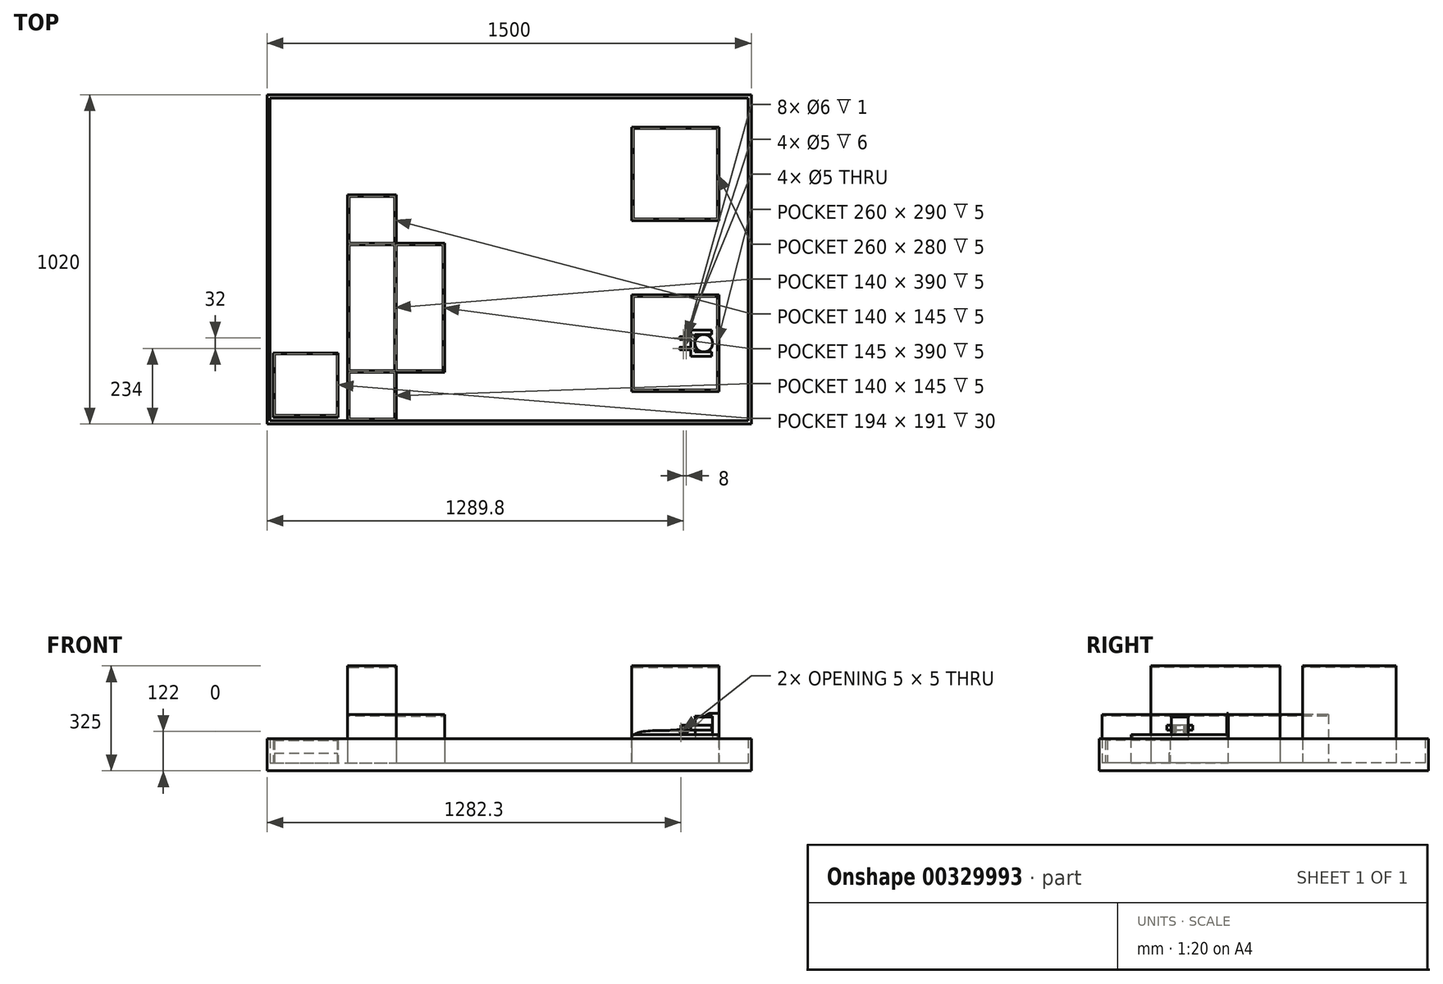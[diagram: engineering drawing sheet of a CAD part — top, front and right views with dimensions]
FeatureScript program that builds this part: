
annotation { "Feature Type Name" : "Feature", "Feature Type Description" : "" }
export const myFeature = defineFeature(function(context is Context, id is Id, definition is map)
    precondition{}
    {
        {
            var Q0;
            Q0=qCreatedBy(makeId("Top.planeOp"),FACE);
            var sketch = newSketch(context, id + "F0", { "sketchPlane" : qUnion([Q0])});
            skCircle(sketch, "E0", {"center": v(0, 0) * mm, "radius": 27.2 * mm});
            skSolve(sketch);
        }
        {
            var Q0;
            Q0=qSketchRegion(id+"F0",true);
            extrude(context, id + "F1", {"entities" : qUnion([Q0]), "depth" : 2.83 * mm});
        }
        {
            var Q0;
            Q0=makeQuery(id+"F1.opExtrude","CAP_FACE",FACE,{"disambiguationData":[OSD([sQuery(id+"F0.wireOp",EDGE,"E0")])],"isStart":false});
            var sketch = newSketch(context, id + "F2", { "sketchPlane" : qUnion([Q0])});
            skCircle(sketch, "E1", {"center": v(0, 0) * mm, "radius": 26.4 * mm});
            skSolve(sketch);
        }
        {
            var Q0;
            Q0=qSketchRegion(id+"F2",true);
            extrude(context, id + "F3", {"entities" : qUnion([Q0]), "operationType" : NewBodyOperationType.ADD, "depth" : 67.36 * mm});
        }
        {
            var Q0;
            Q0=makeQuery(id+"F3.opExtrude","CAP_FACE",FACE,{"disambiguationData":[OSD([sQuery(id+"F2.wireOp",EDGE,"E1")])],"isStart":false});
            var sketch = newSketch(context, id + "F4", { "sketchPlane" : qUnion([Q0])});
            skCircle(sketch, "E2", {"center": v(0, 0) * mm, "radius": 27.2 * mm});
            skSolve(sketch);
        }
        {
            var Q0;
            Q0=qSketchRegion(id+"F4",true);
            extrude(context, id + "F5", {"entities" : qUnion([Q0]), "operationType" : NewBodyOperationType.ADD, "depth" : 2.83 * mm});
        }
        {
            var Q0;
            Q0=makeQuery(id+"F5.opExtrude","CAP_FACE",FACE,{"disambiguationData":[OSD([sQuery(id+"F4.wireOp",EDGE,"E2")])],"isStart":false});
            var sketch = newSketch(context, id + "F6", { "sketchPlane" : qUnion([Q0])});
            skSolve(sketch);
        }
        {
            var Q0;
            Q0=qCreatedBy(makeId("Top.planeOp"),FACE);
            cPlane(context, id + "F7", {"entities" : qUnion([Q0]), "cplaneType" : CPlaneType.OFFSET, "offset" : 25 * mm, "width" : 150 * mm, "height" : 150 * mm});
        }
        {
            var Q0;
            Q0=makeQuery(id+"F6.imprint","IMPRINT",FACE,{"disambiguationData":[TD([[makeQuery(id+"F6.imprint","IMPRINT",EDGE,{"derivedFrom":makeQuery(id+"F5.opExtrude","CAP_EDGE",EDGE,{"disambiguationData":[OSD([sQuery(id+"F4.wireOp",EDGE,"E2")])],"isStart":false})}),1.0]])]});
            var sketch = newSketch(context, id + "F8", { "sketchPlane" : qUnion([Q0])});
            skSolve(sketch);
        }
        {
            var Q0;
            Q0=qCreatedBy(makeId("Top.planeOp"),FACE);
            var sketch = newSketch(context, id + "F9", { "sketchPlane" : qUnion([Q0])});
            skLineSegment(sketch, "E3.bottom", {"start": v(-222.8, -150) * mm, "end": v(47.2, -150) * mm});
            skLineSegment(sketch, "E3.top", {"start": v(-222.8, 150) * mm, "end": v(47.2, 150) * mm});
            skLineSegment(sketch, "E3.left", {"start": v(-222.8, -150) * mm, "end": v(-222.8, 150) * mm});
            skLineSegment(sketch, "E3.right", {"start": v(47.2, -150) * mm, "end": v(47.2, 150) * mm});
            skSolve(sketch);
        }
        {
            var Q0;
            Q0=qSketchRegion(id+"F9",true);
            extrude(context, id + "F10", {"entities" : qUnion([Q0]), "oppositeDirection" : true, "depth" : 72 * mm});
        }
        {
            var Q0;
            Q0=makeQuery(id+"F10.opExtrude","CAP_FACE",FACE,{"disambiguationData":[OSD([sQuery(id+"F9.wireOp",EDGE,"E3.bottom"),sQuery(id+"F9.wireOp",EDGE,"E3.top"),sQuery(id+"F9.wireOp",EDGE,"E3.left"),sQuery(id+"F9.wireOp",EDGE,"E3.right")])],"isStart":true});
            var sketch = newSketch(context, id + "F11", { "sketchPlane" : qUnion([Q0])});
            skLineSegment(sketch, "E4.bottom", {"start": v(-222.8, -150) * mm, "end": v(47.2, -150) * mm});
            skLineSegment(sketch, "E4.top", {"start": v(-222.8, -145) * mm, "end": v(42.2, -145) * mm});
            skLineSegment(sketch, "E4.left", {"start": v(-222.8, -150) * mm, "end": v(-222.8, -145) * mm});
            skLineSegment(sketch, "E5.bottom", {"start": v(47.2, 150) * mm, "end": v(42.2, 150) * mm});
            skLineSegment(sketch, "E5.left", {"start": v(47.2, 150) * mm, "end": v(47.2, -150) * mm});
            skLineSegment(sketch, "E5.right", {"start": v(42.2, 150) * mm, "end": v(42.2, -145) * mm});
            skSolve(sketch);
        }
        {
            var Q0;
            Q0=qSketchRegion(id+"F11",true);
            extrude(context, id + "F12", {"entities" : qUnion([Q0]), "operationType" : NewBodyOperationType.ADD, "depth" : 15 * mm});
        }
        {
            var Q0;
            Q0=makeQuery(id+"F12.boolean.opBoolean","MERGE",FACE,{"derivedFrom":[makeQuery(id+"F10.opExtrude","SWEPT_FACE",FACE,{"disambiguationData":[OSD([sQuery(id+"F9.wireOp",EDGE,"E3.top")])]}),makeQuery(id+"F12.opExtrude","SWEPT_FACE",FACE,{"disambiguationData":[OSD([sQuery(id+"F11.wireOp",EDGE,"E5.bottom")])]})]});
            var sketch = newSketch(context, id + "F13", { "sketchPlane" : qUnion([Q0])});
            skLineSegment(sketch, "E6", {"start": v(-47.2, 81.36) * mm, "end": v(-21.31, 81.36) * mm});
            skFitSpline(sketch, "E7", {"points": [v(-21.31, 81.36) * mm, v(15.24, 52.01) * mm, v(114.14, 28.17) * mm, v(222.8, 0) * mm], "startDerivative": vector(181.02, 0.3) * mm, "endDerivative": vector(-1.73, -239.85) * mm});
            skLineSegment(sketch, "E8", {"start": v(-47.2, 81.36) * mm, "end": v(-47.2, -72) * mm});
            skLineSegment(sketch, "E9", {"start": v(-47.2, -72) * mm, "end": v(222.8, -72) * mm});
            skLineSegment(sketch, "E10", {"start": v(222.8, -72) * mm, "end": v(222.8, 0) * mm});
            skSolve(sketch);
        }
        {
            var Q0;
            Q0=qSketchRegion(id+"F13",true);
            extrude(context, id + "F14", {"entities" : qUnion([Q0]), "operationType" : NewBodyOperationType.ADD, "oppositeDirection" : true, "depth" : 5 * mm});
        }
        {
            var Q0;
            Q0=makeQuery(id+"F10.opExtrude","CAP_FACE",FACE,{"disambiguationData":[OSD([sQuery(id+"F9.wireOp",EDGE,"E3.bottom"),sQuery(id+"F9.wireOp",EDGE,"E3.top"),sQuery(id+"F9.wireOp",EDGE,"E3.left"),sQuery(id+"F9.wireOp",EDGE,"E3.right")])],"isStart":true});
            var sketch = newSketch(context, id + "F15", { "sketchPlane" : qUnion([Q0])});
            skLineSegment(sketch, "E11.bottom", {"start": v(-222.8, 145) * mm, "end": v(-217.8, 145) * mm});
            skLineSegment(sketch, "E11.top", {"start": v(-222.8, -145) * mm, "end": v(-217.8, -145) * mm});
            skLineSegment(sketch, "E11.left", {"start": v(-222.8, 145) * mm, "end": v(-222.8, -145) * mm});
            skLineSegment(sketch, "E11.right", {"start": v(-217.8, 145) * mm, "end": v(-217.8, -145) * mm});
            skSolve(sketch);
        }
        {
            var Q0;
            Q0=qSketchRegion(id+"F15",true);
            extrude(context, id + "F16", {"entities" : qUnion([Q0]), "operationType" : NewBodyOperationType.ADD, "depth" : 5 * mm});
        }
        {
            var Q0;
            Q0=makeQuery(id+"F10.opExtrude","CAP_FACE",FACE,{"disambiguationData":[OSD([sQuery(id+"F9.wireOp",EDGE,"E3.bottom"),sQuery(id+"F9.wireOp",EDGE,"E3.top"),sQuery(id+"F9.wireOp",EDGE,"E3.left"),sQuery(id+"F9.wireOp",EDGE,"E3.right")])],"isStart":false});
            var sketch = newSketch(context, id + "F17", { "sketchPlane" : qUnion([Q0])});
            skLineSegment(sketch, "E12.bottom", {"start": v(147.2, 250) * mm, "end": v(-1352.8, 250) * mm});
            skLineSegment(sketch, "E12.top", {"start": v(147.2, -770) * mm, "end": v(-1352.8, -770) * mm});
            skLineSegment(sketch, "E12.left", {"start": v(147.2, 250) * mm, "end": v(147.2, -770) * mm});
            skLineSegment(sketch, "E12.right", {"start": v(-1352.8, 250) * mm, "end": v(-1352.8, -770) * mm});
            skSolve(sketch);
        }
        {
            var Q0;
            Q0=qSketchRegion(id+"F17",true);
            extrude(context, id + "F18", {"entities" : qUnion([Q0]), "operationType" : NewBodyOperationType.ADD, "depth" : 25 * mm});
        }
        {
            var Q0;
            Q0=makeQuery(id+"F18.opExtrude","CAP_FACE",FACE,{"disambiguationData":[OSD([sQuery(id+"F17.wireOp",EDGE,"E12.bottom"),sQuery(id+"F17.wireOp",EDGE,"E12.top"),sQuery(id+"F17.wireOp",EDGE,"E12.left"),sQuery(id+"F17.wireOp",EDGE,"E12.right")])],"isStart":true});
            var sketch = newSketch(context, id + "F19", { "sketchPlane" : qUnion([Q0])});
            skLineSegment(sketch, "E13.bottom", {"start": v(-222.8, 670) * mm, "end": v(47.2, 670) * mm});
            skLineSegment(sketch, "E13.top", {"start": v(-222.8, 380) * mm, "end": v(47.2, 380) * mm});
            skLineSegment(sketch, "E13.left", {"start": v(-222.8, 670) * mm, "end": v(-222.8, 380) * mm});
            skLineSegment(sketch, "E13.right", {"start": v(47.2, 670) * mm, "end": v(47.2, 380) * mm});
            skSolve(sketch);
        }
        {
            var Q0;
            Q0=qSketchRegion(id+"F19",true);
            extrude(context, id + "F20", {"entities" : qUnion([Q0]), "operationType" : NewBodyOperationType.ADD, "depth" : 300 * mm});
        }
        {
            var Q0;
            Q0=makeQuery(id+"F20.opExtrude","CAP_FACE",FACE,{"disambiguationData":[OSD([sQuery(id+"F19.wireOp",EDGE,"E13.bottom"),sQuery(id+"F19.wireOp",EDGE,"E13.top"),sQuery(id+"F19.wireOp",EDGE,"E13.left"),sQuery(id+"F19.wireOp",EDGE,"E13.right")])],"isStart":false});
            var sketch = newSketch(context, id + "F21", { "sketchPlane" : qUnion([Q0])});
            skLineSegment(sketch, "E14.bottom", {"start": v(-217.8, 665) * mm, "end": v(42.2, 665) * mm});
            skLineSegment(sketch, "E14.top", {"start": v(-217.8, 385) * mm, "end": v(42.2, 385) * mm});
            skLineSegment(sketch, "E14.left", {"start": v(-217.8, 665) * mm, "end": v(-217.8, 385) * mm});
            skLineSegment(sketch, "E14.right", {"start": v(42.2, 665) * mm, "end": v(42.2, 385) * mm});
            skSolve(sketch);
        }
        {
            var Q0;
            Q0=qSketchRegion(id+"F21",true);
            extrude(context, id + "F22", {"entities" : qUnion([Q0]), "operationType" : NewBodyOperationType.REMOVE, "oppositeDirection" : true, "depth" : 5 * mm});
        }
        {
            var Q0;
            Q0=makeQuery(id+"F18.opExtrude","CAP_FACE",FACE,{"disambiguationData":[OSD([sQuery(id+"F17.wireOp",EDGE,"E12.bottom"),sQuery(id+"F17.wireOp",EDGE,"E12.top"),sQuery(id+"F17.wireOp",EDGE,"E12.left"),sQuery(id+"F17.wireOp",EDGE,"E12.right")])],"isStart":true});
            var sketch = newSketch(context, id + "F23", { "sketchPlane" : qUnion([Q0])});
            skLineSegment(sketch, "E15.bottom", {"start": v(-1352.8, 770) * mm, "end": v(147.2, 770) * mm});
            skLineSegment(sketch, "E15.top", {"start": v(-1352.8, -250) * mm, "end": v(147.2, -250) * mm});
            skLineSegment(sketch, "E15.left", {"start": v(-1352.8, 770) * mm, "end": v(-1352.8, -250) * mm});
            skLineSegment(sketch, "E15.right", {"start": v(147.2, 770) * mm, "end": v(147.2, -250) * mm});
            skLineSegment(sketch, "E16.bottom", {"start": v(-1342.8, 760) * mm, "end": v(137.2, 760) * mm});
            skLineSegment(sketch, "E16.top", {"start": v(-1342.8, -240) * mm, "end": v(137.2, -240) * mm});
            skLineSegment(sketch, "E16.left", {"start": v(-1342.8, 760) * mm, "end": v(-1342.8, -240) * mm});
            skLineSegment(sketch, "E16.right", {"start": v(137.2, 760) * mm, "end": v(137.2, -240) * mm});
            skSolve(sketch);
        }
        {
            var Q0;
            Q0=qSketchRegion(id+"F23",true);
            extrude(context, id + "F24", {"entities" : qUnion([Q0]), "operationType" : NewBodyOperationType.ADD, "depth" : 75 * mm});
        }
        {
            var Q0;
            Q0=makeQuery(id+"F18.opExtrude","CAP_FACE",FACE,{"disambiguationData":[OSD([sQuery(id+"F17.wireOp",EDGE,"E12.bottom"),sQuery(id+"F17.wireOp",EDGE,"E12.top"),sQuery(id+"F17.wireOp",EDGE,"E12.left"),sQuery(id+"F17.wireOp",EDGE,"E12.right")])],"isStart":true});
            var sketch = newSketch(context, id + "F25", { "sketchPlane" : qUnion([Q0])});
            skLineSegment(sketch, "E17.bottom", {"start": v(-1102.8, 460) * mm, "end": v(-952.8, 460) * mm});
            skLineSegment(sketch, "E17.top", {"start": v(-1102.8, -240) * mm, "end": v(-952.8, -240) * mm});
            skLineSegment(sketch, "E17.left", {"start": v(-1102.8, 460) * mm, "end": v(-1102.8, -240) * mm});
            skLineSegment(sketch, "E17.right", {"start": v(-952.8, 460) * mm, "end": v(-952.8, 310) * mm});
            skLineSegment(sketch, "E18.bottom", {"start": v(-952.8, 310) * mm, "end": v(-802.8, 310) * mm});
            skLineSegment(sketch, "E18.top", {"start": v(-952.8, -90) * mm, "end": v(-802.8, -90) * mm});
            skLineSegment(sketch, "E18.right", {"start": v(-802.8, 310) * mm, "end": v(-802.8, -90) * mm});
            skLineSegment(sketch, "E19.trimOffspring", {"start": v(-952.8, -90) * mm, "end": v(-952.8, -240) * mm});
            skSolve(sketch);
        }
        {
            var Q0;
            Q0=qSketchRegion(id+"F25",true);
            extrude(context, id + "F26", {"entities" : qUnion([Q0]), "operationType" : NewBodyOperationType.ADD, "depth" : 150 * mm});
        }
        {
            var Q0;
            Q0=makeQuery(id+"F26.opExtrude","CAP_FACE",FACE,{"disambiguationData":[OSD([sQuery(id+"F25.wireOp",EDGE,"E17.bottom"),sQuery(id+"F25.wireOp",EDGE,"E17.top"),sQuery(id+"F25.wireOp",EDGE,"E17.left"),sQuery(id+"F25.wireOp",EDGE,"E17.right"),sQuery(id+"F25.wireOp",EDGE,"E18.bottom"),sQuery(id+"F25.wireOp",EDGE,"E18.top"),sQuery(id+"F25.wireOp",EDGE,"E18.right"),sQuery(id+"F25.wireOp",EDGE,"E19.trimOffspring")])],"isStart":false});
            var sketch = newSketch(context, id + "F27", { "sketchPlane" : qUnion([Q0])});
            skLineSegment(sketch, "E20.bottom", {"start": v(-952.8, 310) * mm, "end": v(-1102.8, 310) * mm});
            skLineSegment(sketch, "E20.top", {"start": v(-952.8, -90) * mm, "end": v(-1102.8, -90) * mm});
            skLineSegment(sketch, "E20.left", {"start": v(-952.8, 310) * mm, "end": v(-952.8, -90) * mm});
            skLineSegment(sketch, "E20.right", {"start": v(-1102.8, 310) * mm, "end": v(-1102.8, -90) * mm});
            skSolve(sketch);
        }
        {
            var Q0;
            Q0=qSketchRegion(id+"F27",true);
            extrude(context, id + "F28", {"entities" : qUnion([Q0]), "operationType" : NewBodyOperationType.ADD, "depth" : 150 * mm});
        }
        {
            var Q0;
            Q0=makeQuery(id+"F28.opExtrude","CAP_FACE",FACE,{"disambiguationData":[OSD([sQuery(id+"F27.wireOp",EDGE,"E20.bottom"),sQuery(id+"F27.wireOp",EDGE,"E20.top"),sQuery(id+"F27.wireOp",EDGE,"E20.left"),sQuery(id+"F27.wireOp",EDGE,"E20.right")])],"isStart":false});
            var sketch = newSketch(context, id + "F29", { "sketchPlane" : qUnion([Q0])});
            skLineSegment(sketch, "E21.bottom", {"start": v(-1097.8, 305) * mm, "end": v(-957.8, 305) * mm});
            skLineSegment(sketch, "E21.top", {"start": v(-1097.8, -85) * mm, "end": v(-957.8, -85) * mm});
            skLineSegment(sketch, "E21.left", {"start": v(-1097.8, 305) * mm, "end": v(-1097.8, -85) * mm});
            skLineSegment(sketch, "E21.right", {"start": v(-957.8, 305) * mm, "end": v(-957.8, -85) * mm});
            skSolve(sketch);
        }
        {
            var Q0;
            Q0=qSketchRegion(id+"F29",true);
            extrude(context, id + "F30", {"entities" : qUnion([Q0]), "operationType" : NewBodyOperationType.REMOVE, "oppositeDirection" : true, "depth" : 5 * mm});
        }
        {
            var Q0;
            {var subQ0=sQuery(id+"F25.wireOp",EDGE,"E17.left");var subQ1=sQuery(id+"F25.wireOp",EDGE,"E18.bottom");var subQ2=sQuery(id+"F25.wireOp",EDGE,"E17.right");var subQ3=sQuery(id+"F25.wireOp",EDGE,"E17.bottom");var subQ4=makeQuery(id+"F26.opExtrude","CAP_FACE",FACE,{"disambiguationData":[OSD([subQ3,sQuery(id+"F25.wireOp",EDGE,"E17.top"),subQ0,subQ2,subQ1,sQuery(id+"F25.wireOp",EDGE,"E18.top"),sQuery(id+"F25.wireOp",EDGE,"E18.right"),sQuery(id+"F25.wireOp",EDGE,"E19.trimOffspring")])],"isStart":false});Q0=makeQuery(id+"F28.boolean.opBoolean","SPLIT",FACE,{"disambiguationData":[TD([makeQuery(id+"F26.opExtrude","SWEPT_FACE",FACE,{"disambiguationData":[OSD([subQ3])]})])],"derivedFrom":subQ4});}
            var sketch = newSketch(context, id + "F31", { "sketchPlane" : qUnion([Q0])});
            skLineSegment(sketch, "E22.bottom", {"start": v(-1097.8, 455) * mm, "end": v(-957.8, 455) * mm});
            skLineSegment(sketch, "E22.top", {"start": v(-1097.8, 310) * mm, "end": v(-957.8, 310) * mm});
            skLineSegment(sketch, "E22.left", {"start": v(-1097.8, 455) * mm, "end": v(-1097.8, 310) * mm});
            skLineSegment(sketch, "E22.right", {"start": v(-957.8, 455) * mm, "end": v(-957.8, 310) * mm});
            skLineSegment(sketch, "E23.bottom", {"start": v(-952.8, 305) * mm, "end": v(-807.8, 305) * mm});
            skLineSegment(sketch, "E23.top", {"start": v(-952.8, -85) * mm, "end": v(-807.8, -85) * mm});
            skLineSegment(sketch, "E23.left", {"start": v(-952.8, 305) * mm, "end": v(-952.8, -85) * mm});
            skLineSegment(sketch, "E23.right", {"start": v(-807.8, 305) * mm, "end": v(-807.8, -85) * mm});
            skLineSegment(sketch, "E24.bottom", {"start": v(-1097.8, -90) * mm, "end": v(-957.8, -90) * mm});
            skLineSegment(sketch, "E24.top", {"start": v(-1097.8, -235) * mm, "end": v(-957.8, -235) * mm});
            skLineSegment(sketch, "E24.left", {"start": v(-1097.8, -90) * mm, "end": v(-1097.8, -235) * mm});
            skLineSegment(sketch, "E24.right", {"start": v(-957.8, -90) * mm, "end": v(-957.8, -235) * mm});
            skSolve(sketch);
        }
        {
            var Q0;
            Q0=qSketchRegion(id+"F31",true);
            extrude(context, id + "F32", {"entities" : qUnion([Q0]), "operationType" : NewBodyOperationType.REMOVE, "oppositeDirection" : true, "depth" : 5 * mm});
        }
        {
            var Q0;
            Q0=qCreatedBy(id+"F7.planeOp",FACE);
            var sketch = newSketch(context, id + "F33", { "sketchPlane" : qUnion([Q0])});
            skLineSegment(sketch, "E25", {"start": v(0, 0) * mm, "end": v(-90, 0) * mm, "construction": true});
            skLineSegment(sketch, "E26.bottom", {"start": v(-74.5, -12) * mm, "end": v(-55, -12) * mm});
            skLineSegment(sketch, "E26.top", {"start": v(-74.5, -20) * mm, "end": v(-55, -20) * mm});
            skLineSegment(sketch, "E26.left", {"start": v(-74.5, -12) * mm, "end": v(-74.5, -13) * mm});
            skPoint(sketch, "E27.visualSharp", {"position": v(-51, -12) * mm});
            skPoint(sketch, "E28.visualSharp", {"position": v(-51, -20) * mm});
            skCircle(sketch, "E29", {"center": v(-55, -16) * mm, "radius": 3 * mm});
            skLineSegment(sketch, "E30", {"start": v(-59, -3.98) * mm, "end": v(-59, -18.08) * mm, "construction": true});
            skCircle(sketch, "E31.MirrorC", {"center": v(-63, -16) * mm, "radius": 3 * mm});
            skLineSegment(sketch, "E32.bottom", {"start": v(-74.5, -13) * mm, "end": v(-65.65, -13) * mm});
            skLineSegment(sketch, "E32.top", {"start": v(-74.5, -19) * mm, "end": v(-65.65, -19) * mm});
            skArc(sketch, "E33", {"start": v(-65.65, -13) * mm, "mid": v(-67, -16) * mm, "end": v(-65.65, -19) * mm});
            skLineSegment(sketch, "E34.trimOffspring", {"start": v(-74.5, -19) * mm, "end": v(-74.5, -20) * mm});
            skArc(sketch, "E35.trimOffspring", {"start": v(-55, -20) * mm, "mid": v(-51, -16) * mm, "end": v(-55, -12) * mm});
            skLineSegment(sketch, "E36.MirrorCS", {"start": v(-74.5, 12) * mm, "end": v(-74.5, 13) * mm});
            skLineSegment(sketch, "E37.MirrorCS", {"start": v(-74.5, 19) * mm, "end": v(-74.5, 20) * mm});
            skPoint(sketch, "E38.MirrorP", {"position": v(-51, 12) * mm});
            skLineSegment(sketch, "E39.MirrorCS", {"start": v(-74.5, 12) * mm, "end": v(-55, 12) * mm});
            skPoint(sketch, "E40.MirrorP", {"position": v(-51, 20) * mm});
            skArc(sketch, "E41.MirrorCS", {"start": v(-65.65, 13) * mm, "mid": v(-67, 16) * mm, "end": v(-65.65, 19) * mm});
            skArc(sketch, "E42.MirrorCS", {"start": v(-55, 20) * mm, "mid": v(-51, 16) * mm, "end": v(-55, 12) * mm});
            skLineSegment(sketch, "E43.MirrorCS", {"start": v(-74.5, 20) * mm, "end": v(-55, 20) * mm});
            skCircle(sketch, "E44.MirrorC", {"center": v(-55, 16) * mm, "radius": 3 * mm});
            skCircle(sketch, "E45.MirrorC", {"center": v(-63, 16) * mm, "radius": 3 * mm});
            skLineSegment(sketch, "E46.MirrorCS", {"start": v(-74.5, 19) * mm, "end": v(-65.65, 19) * mm});
            skLineSegment(sketch, "E47.MirrorCS", {"start": v(-74.5, 13) * mm, "end": v(-65.65, 13) * mm});
            skSolve(sketch);
        }
        {
            var Q0;
            Q0=qSketchRegion(id+"F33",true);
            var Q1;
            Q1=qSketchRegion(id+"F36",true);
            extrude(context, id + "F34", {"entities" : qUnion([Q0, Q1]), "endBound" : BoundingType.SYMMETRIC, "depth" : 8 * mm});
        }
        {
            var Q0;
            Q0=makeQuery(id+"F34.opExtrude","CAP_EDGE",EDGE,{"disambiguationData":[OSD([sQuery(id+"F33.wireOp",EDGE,"E34.trimOffspring")])],"isStart":false});
            var Q1;
            Q1=makeQuery(id+"F34.opExtrude","CAP_EDGE",EDGE,{"disambiguationData":[OSD([sQuery(id+"F33.wireOp",EDGE,"E26.left")])],"isStart":false});
            var Q2;
            Q2=makeQuery(id+"F34.opExtrude","CAP_EDGE",EDGE,{"disambiguationData":[OSD([sQuery(id+"F33.wireOp",EDGE,"E34.trimOffspring")])],"isStart":true});
            var Q3;
            Q3=makeQuery(id+"F34.opExtrude","CAP_EDGE",EDGE,{"disambiguationData":[OSD([sQuery(id+"F33.wireOp",EDGE,"E26.left")])],"isStart":true});
            var Q4;
            Q4=makeQuery(id+"F34.opExtrude","CAP_EDGE",EDGE,{"disambiguationData":[OSD([sQuery(id+"F33.wireOp",EDGE,"E36.MirrorCS")])],"isStart":false});
            var Q5;
            Q5=makeQuery(id+"F34.opExtrude","CAP_EDGE",EDGE,{"disambiguationData":[OSD([sQuery(id+"F33.wireOp",EDGE,"E37.MirrorCS")])],"isStart":false});
            var Q6;
            Q6=makeQuery(id+"F34.opExtrude","CAP_EDGE",EDGE,{"disambiguationData":[OSD([sQuery(id+"F33.wireOp",EDGE,"E37.MirrorCS")])],"isStart":true});
            var Q7;
            Q7=makeQuery(id+"F34.opExtrude","CAP_EDGE",EDGE,{"disambiguationData":[OSD([sQuery(id+"F33.wireOp",EDGE,"E36.MirrorCS")])],"isStart":true});
            fillet(context, id + "F35", {"entities" : qUnion([Q0, Q1, Q2, Q3, Q4, Q5, Q6, Q7]), "radius" : 4 * mm, "tangentPropagation" : true, "allowEdgeOverflow" : false});
        }
        {
            var Q0;
            Q0=makeQuery(id+"F34.opExtrude","SWEPT_FACE",FACE,{"disambiguationData":[OSD([sQuery(id+"F33.wireOp",EDGE,"E26.top")])]});
            var sketch = newSketch(context, id + "F36", { "sketchPlane" : qUnion([Q0])});
            skCircle(sketch, "E48", {"center": v(-70.5, 25) * mm, "radius": 3 * mm});
            skSolve(sketch);
        }
        {
            var Q0;
            Q0=qSketchRegion(id+"F36",true);
            var Q1;
            Q1=makeQuery(id+"F34.opExtrude","SWEPT_FACE",FACE,{"disambiguationData":[OSD([sQuery(id+"F33.wireOp",EDGE,"E26.bottom")])]});
            extrude(context, id + "F37", {"entities" : qUnion([Q0]), "operationType" : NewBodyOperationType.ADD, "endBound" : BoundingType.UP_TO_SURFACE, "oppositeDirection" : true, "endBoundEntityFace" : qUnion([Q1]), "depth" : 25 * mm});
        }
        {
            var Q0;
            Q0=makeQuery(id+"F34.opExtrude","SWEPT_FACE",FACE,{"disambiguationData":[OSD([sQuery(id+"F33.wireOp",EDGE,"E43.MirrorCS")])]});
            var sketch = newSketch(context, id + "F38", { "sketchPlane" : qUnion([Q0])});
            skCircle(sketch, "E49", {"center": v(70.5, 25) * mm, "radius": 3 * mm});
            skSolve(sketch);
        }
        {
            var Q0;
            Q0=qSketchRegion(id+"F38",true);
            var Q1;
            Q1=makeQuery(id+"F34.opExtrude","SWEPT_FACE",FACE,{"disambiguationData":[OSD([sQuery(id+"F33.wireOp",EDGE,"E39.MirrorCS")])]});
            extrude(context, id + "F39", {"entities" : qUnion([Q0]), "operationType" : NewBodyOperationType.ADD, "endBound" : BoundingType.UP_TO_SURFACE, "oppositeDirection" : true, "endBoundEntityFace" : qUnion([Q1]), "depth" : 25 * mm});
        }
        {
            var Q0;
            Q0=qCreatedBy(id+"F7.planeOp",FACE);
            var sketch = newSketch(context, id + "F40", { "sketchPlane" : qUnion([Q0])});
            skCircle(sketch, "E50", {"center": v(-55, 16) * mm, "radius": 3 * mm});
            skCircle(sketch, "E51", {"center": v(-63, 16) * mm, "radius": 2.5 * mm});
            skCircle(sketch, "E52", {"center": v(-63, 16) * mm, "radius": 3 * mm});
            skCircle(sketch, "E53", {"center": v(-55, 16) * mm, "radius": 2.5 * mm});
            skSolve(sketch);
        }
        {
            var Q0;
            Q0=qSketchRegion(id+"F40",true);
            extrude(context, id + "F41", {"entities" : qUnion([Q0]), "operationType" : NewBodyOperationType.ADD, "endBound" : BoundingType.SYMMETRIC, "depth" : 6 * mm});
        }
        {
            var Q0;
            Q0=qCreatedBy(id+"F7.planeOp",FACE);
            var sketch = newSketch(context, id + "F42", { "sketchPlane" : qUnion([Q0])});
            skCircle(sketch, "E54", {"center": v(-63, -16) * mm, "radius": 2.5 * mm});
            skCircle(sketch, "E55", {"center": v(-63, -16) * mm, "radius": 3 * mm});
            skCircle(sketch, "E56", {"center": v(-55, -16) * mm, "radius": 2.5 * mm});
            skCircle(sketch, "E57", {"center": v(-55, -16) * mm, "radius": 3 * mm});
            skSolve(sketch);
        }
        {
            var Q0;
            Q0=qSketchRegion(id+"F42",true);
            extrude(context, id + "F43", {"entities" : qUnion([Q0]), "operationType" : NewBodyOperationType.ADD, "endBound" : BoundingType.SYMMETRIC, "depth" : 6 * mm});
        }
        {
            var Q0;
            Q0=makeQuery(id+"F34.opExtrude","SWEPT_FACE",FACE,{"disambiguationData":[OSD([sQuery(id+"F33.wireOp",EDGE,"E43.MirrorCS")])]});
            var sketch = newSketch(context, id + "F44", { "sketchPlane" : qUnion([Q0])});
            skArc(sketch, "E58", {"start": v(71.5, 27.3) * mm, "mid": v(70.5, 27.5) * mm, "end": v(69.5, 27.3) * mm});
            skLineSegment(sketch, "E59.bottom", {"start": v(68.2, 26) * mm, "end": v(69.5, 26) * mm});
            skLineSegment(sketch, "E59.top", {"start": v(68.2, 24) * mm, "end": v(69.5, 24) * mm});
            skLineSegment(sketch, "E60.left", {"start": v(71.5, 27.3) * mm, "end": v(71.5, 26) * mm});
            skLineSegment(sketch, "E60.right", {"start": v(69.5, 27.3) * mm, "end": v(69.5, 26) * mm});
            skPoint(sketch, "E61.orphan", {"position": v(69.5, 27.8) * mm});
            skPoint(sketch, "E62.orphan", {"position": v(71.5, 27.8) * mm});
            skArc(sketch, "E63.trimOffspring", {"start": v(68.2, 26) * mm, "mid": v(68, 25) * mm, "end": v(68.2, 24) * mm});
            skPoint(sketch, "E59.left.start.orphan", {"position": v(67.32, 26) * mm});
            skPoint(sketch, "E64.orphan", {"position": v(67.32, 24) * mm});
            skArc(sketch, "E65.trimOffspring", {"start": v(69.5, 22.7) * mm, "mid": v(70.5, 22.5) * mm, "end": v(71.5, 22.7) * mm});
            skLineSegment(sketch, "E66.trimOffspring", {"start": v(69.5, 24) * mm, "end": v(69.5, 22.7) * mm});
            skLineSegment(sketch, "E67.trimOffspring", {"start": v(71.5, 26) * mm, "end": v(72.8, 26) * mm});
            skLineSegment(sketch, "E68.trimOffspring", {"start": v(71.5, 24) * mm, "end": v(71.5, 22.7) * mm});
            skLineSegment(sketch, "E69.trimOffspring", {"start": v(71.5, 24) * mm, "end": v(72.8, 24) * mm});
            skPoint(sketch, "E60.top.end.orphan", {"position": v(69.5, 22.2) * mm});
            skPoint(sketch, "E70.orphan", {"position": v(71.5, 22.2) * mm});
            skPoint(sketch, "E59.right.end.orphan", {"position": v(73.68, 24) * mm});
            skPoint(sketch, "E71.orphan", {"position": v(73.68, 26) * mm});
            skArc(sketch, "E72.trimOffspring", {"start": v(72.8, 24) * mm, "mid": v(73, 25) * mm, "end": v(72.8, 26) * mm});
            skSolve(sketch);
        }
        {
            var Q0;
            Q0=qSketchRegion(id+"F44",true);
            extrude(context, id + "F45", {"entities" : qUnion([Q0]), "operationType" : NewBodyOperationType.REMOVE, "endBound" : BoundingType.THROUGH_ALL, "oppositeDirection" : true, "depth" : 25 * mm});
        }
        {
            var Q0;
            Q0=makeQuery(id+"F18.opExtrude","CAP_FACE",FACE,{"disambiguationData":[OSD([sQuery(id+"F17.wireOp",EDGE,"E12.bottom"),sQuery(id+"F17.wireOp",EDGE,"E12.top"),sQuery(id+"F17.wireOp",EDGE,"E12.left"),sQuery(id+"F17.wireOp",EDGE,"E12.right")])],"isStart":true});
            var sketch = newSketch(context, id + "F46", { "sketchPlane" : qUnion([Q0])});
            skLineSegment(sketch, "E73.bottom", {"start": v(-1332.8, -30) * mm, "end": v(-1132.8, -30) * mm});
            skLineSegment(sketch, "E73.top", {"start": v(-1332.8, -230) * mm, "end": v(-1132.8, -230) * mm});
            skLineSegment(sketch, "E73.left", {"start": v(-1332.8, -30) * mm, "end": v(-1332.8, -230) * mm});
            skLineSegment(sketch, "E73.right", {"start": v(-1132.8, -30) * mm, "end": v(-1132.8, -230) * mm});
            skLineSegment(sketch, "E74.bottom", {"start": v(-1329.8, -33) * mm, "end": v(-1135.8, -33) * mm});
            skLineSegment(sketch, "E74.top", {"start": v(-1329.8, -224) * mm, "end": v(-1135.8, -224) * mm});
            skLineSegment(sketch, "E74.left", {"start": v(-1329.8, -33) * mm, "end": v(-1329.8, -224) * mm});
            skLineSegment(sketch, "E74.right", {"start": v(-1135.8, -33) * mm, "end": v(-1135.8, -224) * mm});
            skSolve(sketch);
        }
        {
            var Q0;
            Q0=qSketchRegion(id+"F46",true);
            extrude(context, id + "F47", {"entities" : qUnion([Q0]), "operationType" : NewBodyOperationType.ADD, "depth" : 30 * mm});
        }
        {
            var Q0;
            Q0=makeQuery(id+"F47.opExtrude","CAP_FACE",FACE,{"disambiguationData":[OSD([sQuery(id+"F46.wireOp",EDGE,"E73.bottom"),sQuery(id+"F46.wireOp",EDGE,"E73.top"),sQuery(id+"F46.wireOp",EDGE,"E73.left"),sQuery(id+"F46.wireOp",EDGE,"E73.right"),sQuery(id+"F46.wireOp",EDGE,"E74.bottom"),sQuery(id+"F46.wireOp",EDGE,"E74.top"),sQuery(id+"F46.wireOp",EDGE,"E74.left"),sQuery(id+"F46.wireOp",EDGE,"E74.right")])],"isStart":false});
            var sketch = newSketch(context, id + "F48", { "sketchPlane" : qUnion([Q0])});
            skLineSegment(sketch, "E75.bottom", {"start": v(-1332.8, -30) * mm, "end": v(-1329.8, -30) * mm});
            skLineSegment(sketch, "E75.top", {"start": v(-1332.8, -230) * mm, "end": v(-1329.8, -230) * mm});
            skLineSegment(sketch, "E75.left", {"start": v(-1332.8, -30) * mm, "end": v(-1332.8, -230) * mm});
            skLineSegment(sketch, "E75.right", {"start": v(-1329.8, -30) * mm, "end": v(-1329.8, -224) * mm});
            skLineSegment(sketch, "E76.bottom", {"start": v(-1329.8, -230) * mm, "end": v(-1135.8, -230) * mm});
            skLineSegment(sketch, "E76.top", {"start": v(-1329.8, -224) * mm, "end": v(-1135.8, -224) * mm});
            skLineSegment(sketch, "E77.bottom", {"start": v(-1135.8, -230) * mm, "end": v(-1132.8, -230) * mm});
            skLineSegment(sketch, "E77.top", {"start": v(-1135.8, -30) * mm, "end": v(-1132.8, -30) * mm});
            skLineSegment(sketch, "E77.left", {"start": v(-1135.8, -224) * mm, "end": v(-1135.8, -30) * mm});
            skLineSegment(sketch, "E77.right", {"start": v(-1132.8, -230) * mm, "end": v(-1132.8, -30) * mm});
            skSolve(sketch);
        }
        {
            var Q0;
            Q0=qSketchRegion(id+"F48",true);
            extrude(context, id + "F49", {"entities" : qUnion([Q0]), "operationType" : NewBodyOperationType.ADD, "depth" : 40 * mm});
        }
        {
            var Q0;
            Q0=makeQuery(id+"F34.opExtrude","CAP_FACE",FACE,{"disambiguationData":[OSD([sQuery(id+"F33.wireOp",EDGE,"E36.MirrorCS"),sQuery(id+"F33.wireOp",EDGE,"E37.MirrorCS"),sQuery(id+"F33.wireOp",EDGE,"E39.MirrorCS"),sQuery(id+"F33.wireOp",EDGE,"E41.MirrorCS"),sQuery(id+"F33.wireOp",EDGE,"E42.MirrorCS"),sQuery(id+"F33.wireOp",EDGE,"E43.MirrorCS"),sQuery(id+"F33.wireOp",EDGE,"E44.MirrorC"),sQuery(id+"F33.wireOp",EDGE,"E45.MirrorC"),sQuery(id+"F33.wireOp",EDGE,"E46.MirrorCS"),sQuery(id+"F33.wireOp",EDGE,"E47.MirrorCS")])],"isStart":false});
            var sketch = newSketch(context, id + "F50", { "sketchPlane" : qUnion([Q0])});
            skLineSegment(sketch, "E78", {"start": v(-70.5, 12) * mm, "end": v(-40.76, 12) * mm});
            skLineSegment(sketch, "E79", {"start": v(-70.5, -12.04) * mm, "end": v(-40.76, -12.04) * mm});
            skLineSegment(sketch, "E80", {"start": v(-70.5, -20.16) * mm, "end": v(-40.76, -20.16) * mm});
            skLineSegment(sketch, "E81", {"start": v(-70.5, 20) * mm, "end": v(-40.76, 20) * mm});
            skLineSegment(sketch, "E82", {"start": v(-40.76, 12) * mm, "end": v(-40.76, -12.04) * mm});
            skLineSegment(sketch, "E83", {"start": v(-40.76, -20.16) * mm, "end": v(-40.76, -40.57) * mm});
            skLineSegment(sketch, "E84", {"start": v(-40.76, -40.57) * mm, "end": v(24.03, -40.57) * mm});
            skLineSegment(sketch, "E85", {"start": v(24.03, -40.57) * mm, "end": v(24.03, -27.13) * mm});
            skLineSegment(sketch, "E86", {"start": v(-28.36, -27.13) * mm, "end": v(-28.36, 27.13) * mm});
            skLineSegment(sketch, "E87", {"start": v(-28.36, -27.13) * mm, "end": v(24.03, -27.13) * mm});
            skPoint(sketch, "E88.orphan", {"position": v(24.03, -13.69) * mm});
            skPoint(sketch, "E89.MirrorCS.start.orphan", {"position": v(-40.76, -13.69) * mm});
            skLineSegment(sketch, "E90", {"start": v(-104.63, 0) * mm, "end": v(11.04, 0) * mm, "construction": true});
            skLineSegment(sketch, "E91.MirrorCS", {"start": v(-28.36, 27.13) * mm, "end": v(24.03, 27.13) * mm});
            skLineSegment(sketch, "E92.MirrorCS", {"start": v(-40.76, 40.57) * mm, "end": v(24.03, 40.57) * mm});
            skLineSegment(sketch, "E93", {"start": v(-40.76, 40.57) * mm, "end": v(-40.76, 20) * mm});
            skLineSegment(sketch, "E94", {"start": v(24.03, 40.57) * mm, "end": v(24.03, 27.13) * mm});
            skLineSegment(sketch, "E95", {"start": v(-70.5, -20.16) * mm, "end": v(-70.5, -12.04) * mm});
            skLineSegment(sketch, "E96", {"start": v(-70.5, 12) * mm, "end": v(-70.5, 20) * mm});
            skCircle(sketch, "E97", {"center": v(-55, 16) * mm, "radius": 2.5 * mm});
            skCircle(sketch, "E98", {"center": v(-63, 16) * mm, "radius": 2.5 * mm});
            skCircle(sketch, "E99", {"center": v(-63, -16) * mm, "radius": 2.5 * mm});
            skCircle(sketch, "E100", {"center": v(-55, -16) * mm, "radius": 2.5 * mm});
            skSolve(sketch);
        }
        {
            var Q0;
            Q0 = qSketchRegion(id + "F50", true);
            extrude(context, id + "F51", {"entities" : qUnion([Q0]), "depth" : 15 * mm});
        }
    });
